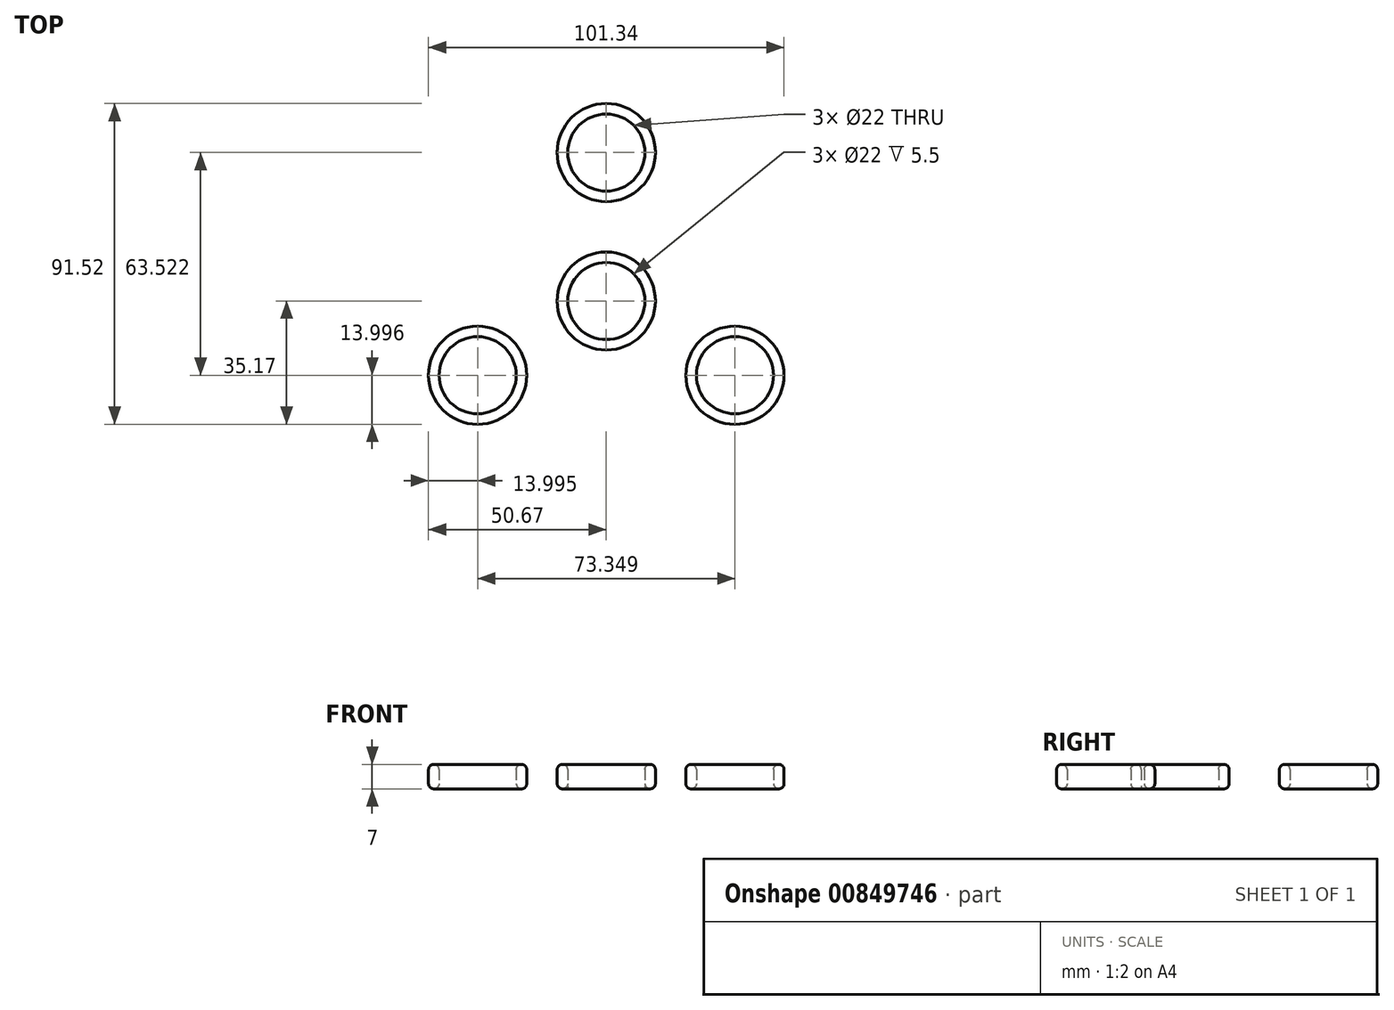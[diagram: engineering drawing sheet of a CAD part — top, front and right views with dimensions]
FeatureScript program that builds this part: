
annotation { "Feature Type Name" : "Feature", "Feature Type Description" : "" }
export const myFeature = defineFeature(function(context is Context, id is Id, definition is map)
    precondition{}
    {
        {
            var Q0;
            Q0=qCreatedBy(makeId("Top.planeOp"),FACE);
            var sketch = newSketch(context, id + "F0", { "sketchPlane" : qUnion([Q0])});
            skCircle(sketch, "E0", {"center": v(0, 0) * mm, "radius": 11 * mm});
            skLineSegment(sketch, "E1", {"start": v(0, 25.34) * mm, "end": v(0, -24.25) * mm, "construction": true});
            skLineSegment(sketch, "E2", {"start": v(0, 16.45) * mm, "end": v(0, -19.25) * mm});
            skCircle(sketch, "E3", {"center": v(0, 0) * mm, "radius": 14 * mm});
            skCircle(sketch, "E4", {"center": v(0, 42.35) * mm, "radius": 11 * mm});
            skCircle(sketch, "E5", {"center": v(0, 42.35) * mm, "radius": 14 * mm});
            skLineSegment(sketch, "E6.bottom", {"start": v(0, 31.35) * mm, "end": v(7.66, 31.35) * mm});
            skLineSegment(sketch, "E6.top", {"start": v(0, 11.72) * mm, "end": v(7.66, 11.72) * mm});
            skLineSegment(sketch, "E6.left", {"start": v(0, 31.35) * mm, "end": v(0, 11.72) * mm});
            skLineSegment(sketch, "E6.right", {"start": v(7.66, 31.35) * mm, "end": v(7.66, 11.72) * mm});
            skLineSegment(sketch, "E7.MirrorCS", {"start": v(0, 31.35) * mm, "end": v(-7.66, 31.35) * mm});
            skLineSegment(sketch, "E8.MirrorCS", {"start": v(-7.66, 31.35) * mm, "end": v(-7.66, 11.72) * mm});
            skLineSegment(sketch, "E9.MirrorCS", {"start": v(0, 11.72) * mm, "end": v(-7.66, 11.72) * mm});
            skSolve(sketch);
        }
        {
            var Q0;
            {var subQ5=sQuery(id+"F0.wireOp",EDGE,"E9.MirrorCS");Q0=makeQuery(id+"F0.imprint","IMPRINT",FACE,{"disambiguationData":[TD([[makeQuery(id+"F0.imprint","IMPRINT",EDGE,{"derivedFrom":subQ5}),1.0]])]});}
            var Q1;
            {var subQ0=sQuery(id+"F0.wireOp",EDGE,"E6.top");Q1=makeQuery(id+"F0.imprint","IMPRINT",FACE,{"disambiguationData":[TD([[makeQuery(id+"F0.imprint","IMPRINT",EDGE,{"derivedFrom":subQ0}),-1.0]])]});}
            var Q2;
            {var subQ0=sQuery(id+"F0.wireOp",EDGE,"E6.left");var subQ1=makeQuery(id+"F0.imprint","IMPRINT",VERTEX,{"derivedFrom":subQ0});Q2=makeQuery(id+"F0.imprint","IMPRINT",FACE,{"disambiguationData":[TD([[makeQuery(id+"F0.imprint","IMPRINT",EDGE,{"disambiguationData":[TD([[subQ1,1.0]])],"derivedFrom":subQ0}),1.0]])]});}
            var Q3;
            Q3=makeQuery(id+"F0.imprint","IMPRINT",FACE,{"disambiguationData":[TD([[makeQuery(id+"F0.imprint","IMPRINT",EDGE,{"derivedFrom":sQuery(id+"F0.wireOp",EDGE,"E4")}),-1.0]])]});
            var Q4;
            {var subQ5=sQuery(id+"F0.wireOp",EDGE,"E7.MirrorCS");Q4=makeQuery(id+"F0.imprint","IMPRINT",FACE,{"disambiguationData":[TD([[makeQuery(id+"F0.imprint","IMPRINT",EDGE,{"derivedFrom":subQ5}),1.0]])]});}
            var Q5;
            {var subQ5=sQuery(id+"F0.wireOp",EDGE,"E6.bottom");Q5=makeQuery(id+"F0.imprint","IMPRINT",FACE,{"disambiguationData":[TD([[makeQuery(id+"F0.imprint","IMPRINT",EDGE,{"derivedFrom":subQ5}),-1.0]])]});}
            var Q6;
            {var subQ0=sQuery(id+"F0.wireOp",EDGE,"E6.left");var subQ1=makeQuery(id+"F0.imprint","IMPRINT",VERTEX,{"derivedFrom":subQ0});Q6=makeQuery(id+"F0.imprint","IMPRINT",FACE,{"disambiguationData":[TD([[makeQuery(id+"F0.imprint","IMPRINT",EDGE,{"disambiguationData":[TD([[subQ1,1.0]])],"derivedFrom":subQ0}),-1.0]])]});}
            var Q7;
            {var subQ0=sQuery(id+"F0.wireOp",EDGE,"E9.MirrorCS");Q7=makeQuery(id+"F0.imprint","IMPRINT",FACE,{"disambiguationData":[TD([[makeQuery(id+"F0.imprint","IMPRINT",EDGE,{"derivedFrom":subQ0}),-1.0]])]});}
            var Q8;
            {var subQ0=sQuery(id+"F0.wireOp",EDGE,"E6.top");Q8=makeQuery(id+"F0.imprint","IMPRINT",FACE,{"disambiguationData":[TD([[makeQuery(id+"F0.imprint","IMPRINT",EDGE,{"derivedFrom":subQ0}),1.0]])]});}
            extrude(context, id + "F1", {"entities" : qUnion([Q0, Q1, Q2, Q3, Q4, Q5, Q6, Q7, Q8]), "depth" : 7 * mm, "offsetDistance" : 25 * mm});
        }
        {
            var Q0;
            Q0=makeQuery(id+"F1.opExtrude","CAP_EDGE",EDGE,{"disambiguationData":[OSD([sQuery(id+"F0.wireOp",EDGE,"E4")])],"isStart":false});
            var Q1;
            Q1=makeQuery(id+"F1.opExtrude","CAP_EDGE",EDGE,{"disambiguationData":[OSD([sQuery(id+"F0.wireOp",EDGE,"E0")])],"isStart":false});
            var Q2;
            Q2=makeQuery(id+"F1.opExtrude","SWEPT_FACE",FACE,{"disambiguationData":[OSD([sQuery(id+"F0.wireOp",EDGE,"E3")])]});
            var Q3;
            Q3=makeQuery(id+"F1.opExtrude","SWEPT_FACE",FACE,{"disambiguationData":[OSD([sQuery(id+"F0.wireOp",EDGE,"E4")])]});
            var Q4;
            Q4=makeQuery(id+"F1.opExtrude","SWEPT_FACE",FACE,{"disambiguationData":[OSD([sQuery(id+"F0.wireOp",EDGE,"E5")])]});
            fillet(context, id + "F2", {"entities" : qUnion([Q0, Q1, Q2, Q3, Q4]), "radius" : 1.5 * mm, "tangentPropagation" : true, "allowEdgeOverflow" : false});
        }
        {
            var Q0;
            Q0=makeQuery(id+"F1.opExtrude","SWEPT_BODY",BODY,{"disambiguationData":[OSD([sQuery(id+"F0.wireOp",EDGE,"E0"),sQuery(id+"F0.wireOp",EDGE,"E3"),sQuery(id+"F0.wireOp",EDGE,"E4"),sQuery(id+"F0.wireOp",EDGE,"E5"),sQuery(id+"F0.wireOp",EDGE,"E6.right"),sQuery(id+"F0.wireOp",EDGE,"E8.MirrorCS")])]});
            var Q1;
            Q1=makeQuery(id+"F1.opExtrude","SWEPT_FACE",FACE,{"disambiguationData":[OSD([sQuery(id+"F0.wireOp",EDGE,"E0")])]});
            circularPattern(context, id + "F3", {"entities" : qUnion([Q0]), "axis" : qUnion([Q1]), "angle" : 360 * degree, "instanceCount" : 3, "equalSpace" : true});
        }
    });
